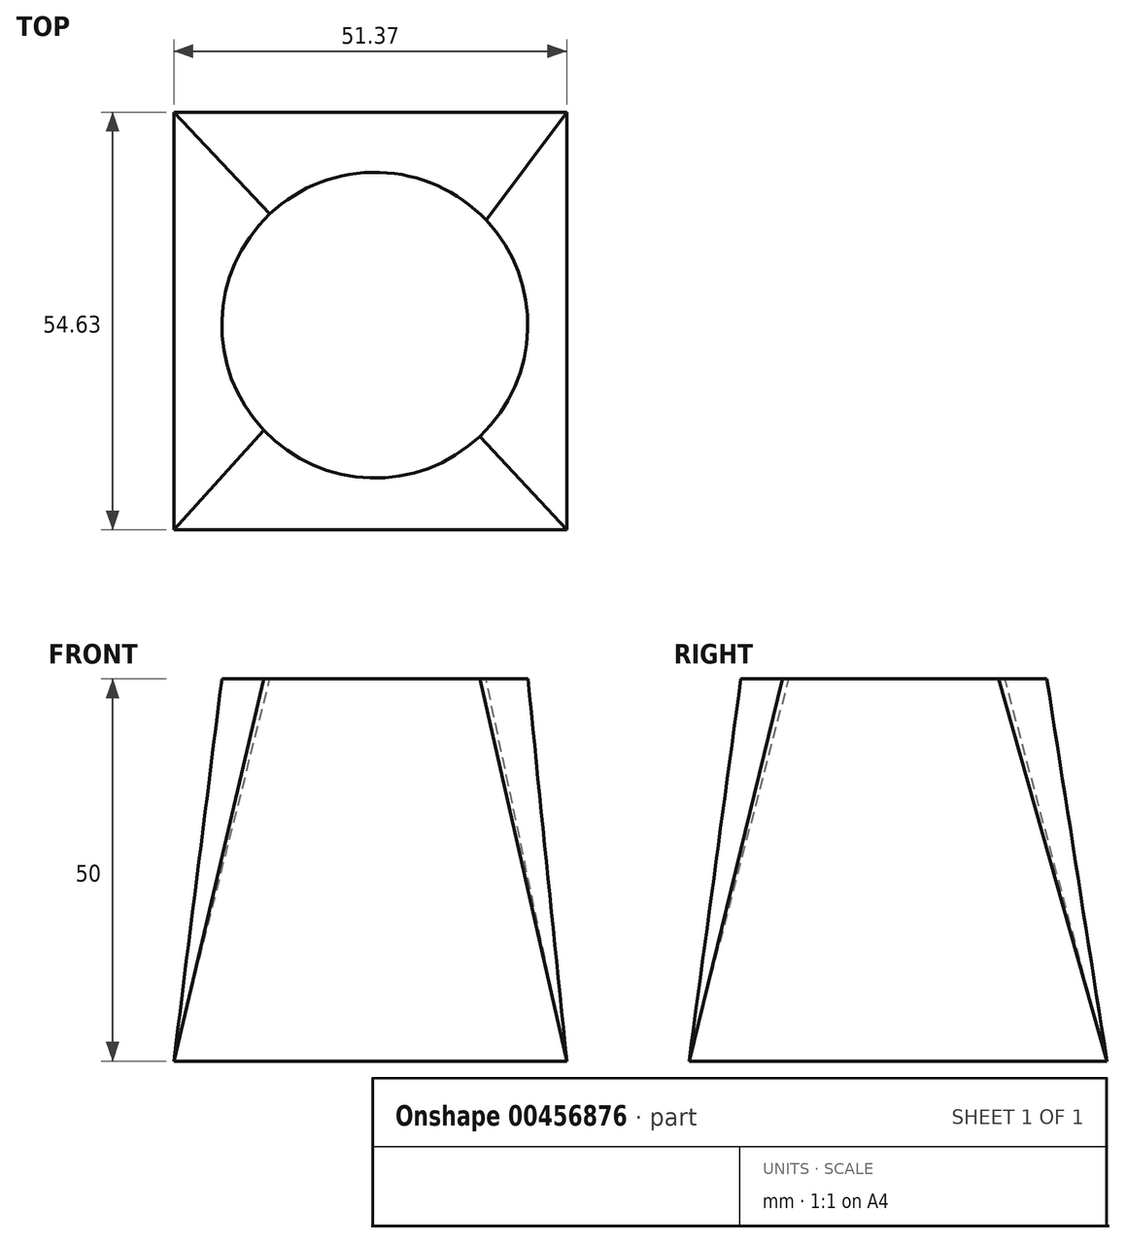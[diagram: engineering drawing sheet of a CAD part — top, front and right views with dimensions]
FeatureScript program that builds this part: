
annotation { "Feature Type Name" : "Feature", "Feature Type Description" : "" }
export const myFeature = defineFeature(function(context is Context, id is Id, definition is map)
    precondition{}
    {
        {
            var Q0;
            Q0=qCreatedBy(makeId("Top.planeOp"),FACE);
            var sketch = newSketch(context, id + "F0", { "sketchPlane" : qUnion([Q0])});
            skLineSegment(sketch, "E0.bottom", {"start": v(0, 0) * mm, "end": v(51.37, 0) * mm});
            skLineSegment(sketch, "E0.top", {"start": v(0, -54.63) * mm, "end": v(51.37, -54.63) * mm});
            skLineSegment(sketch, "E0.left", {"start": v(0, 0) * mm, "end": v(0, -54.63) * mm});
            skLineSegment(sketch, "E0.right", {"start": v(51.37, 0) * mm, "end": v(51.37, -54.63) * mm});
            skSolve(sketch);
        }
        {
            var Q0;
            Q0=qCreatedBy(makeId("Top.planeOp"),FACE);
            cPlane(context, id + "F1", {"entities" : qUnion([Q0]), "cplaneType" : CPlaneType.OFFSET, "offset" : 50 * mm, "width" : 150 * mm, "height" : 150 * mm});
        }
        {
            var Q0;
            Q0=qCreatedBy(id+"F1.planeOp",FACE);
            var sketch = newSketch(context, id + "F2", { "sketchPlane" : qUnion([Q0])});
            skCircle(sketch, "E1", {"center": v(26.3, -27.86) * mm, "radius": 20 * mm});
            skSolve(sketch);
        }
        {
            var Q0;
            Q0 = qSketchRegion(id + "F0", true);
            var Q1;
            Q1 = qSketchRegion(id + "F2", true);
            loft(context, id + "F3", {"sheetProfilesArray" : [{ "sheetProfileEntities" : qUnion([Q0]) }, { "sheetProfileEntities" : qUnion([Q1]) }]});
        }
    });
